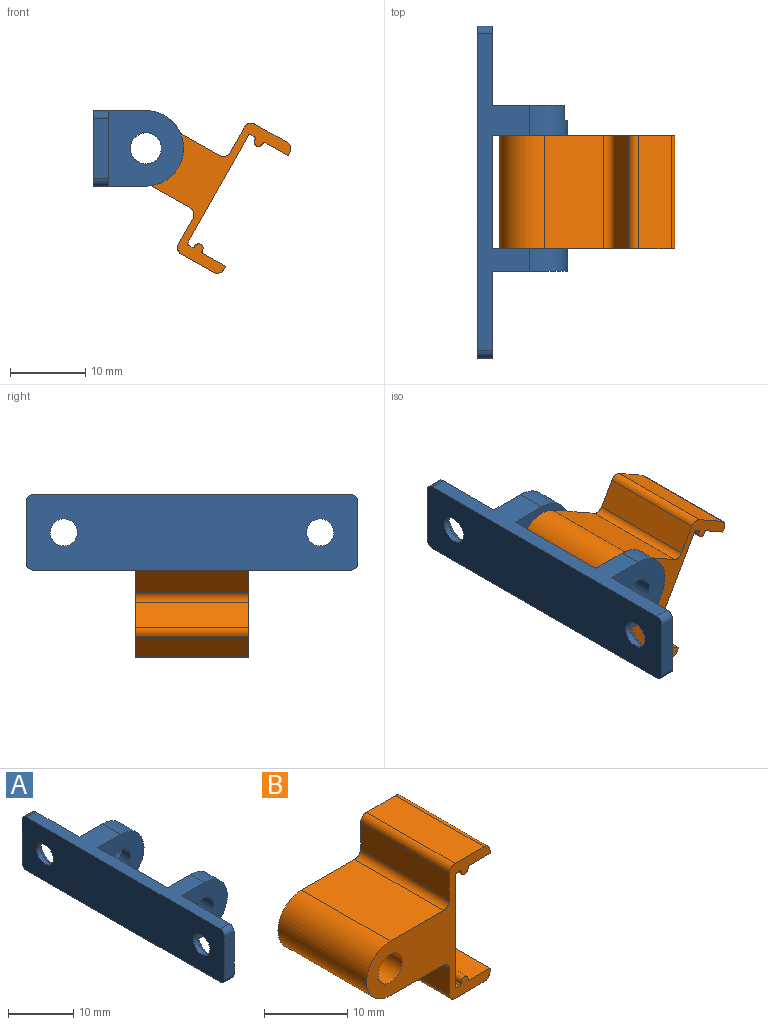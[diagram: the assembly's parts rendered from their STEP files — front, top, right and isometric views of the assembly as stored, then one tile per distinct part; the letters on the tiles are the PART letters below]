
ASSEMBLY  parts=2 mates=1
PART A: 32 faces, bbox 12x44x10 mm
  f0: plane 15.05x10mm, normal (1,0,0), area 150.5mm2, adj f3,f7,f17,f29
  f1: plane 10x9.58mm, normal (0,1,0), area 42.1mm2, adj f2,f3,f7,f18,f19,f20,f21,f22
  f2: plane 10.48x10mm, normal (1,0,0), area 76mm2, adj f1,f3,f7,f12,f13,f14,f16
  f3: plane 42x7mm, normal (0,0,1), area 119mm2, adj f0,f1,f2,f4,f8,f9,f12,f17
  f4: cylinder r=1mm len=2mm, axis (-1,0,0), area 3.1mm2, adj f3,f5,f8,f9
  f5: plane 8x2mm, normal (0,-1,0), area 16mm2, adj f4,f6,f8,f9
  f6: cylinder r=1mm len=2mm, axis (-1,0,0), area 3.1mm2, adj f5,f7,f8,f9
  f7: plane 42x7mm, normal (0,0,-1), area 119mm2, adj f0,f1,f2,f6,f8,f9,f14,f17
  f8: plane 11.48x10mm, normal (1,0,0), area 86mm2, adj f3,f4,f5,f6,f7,f11,f28
  f9: plane 44x10mm, normal (-1,0,0), area 418.8mm2, adj f3,f4,f5,f6,f7,f10,f12,f13
  f10: cylinder r=1.8mm len=3.6mm, axis (1,0,0), area 9mm2, adj f9,f11
  f11: cone r=1.8mm half-angle=45deg, axis (1,0,0), area 25.6mm2, adj f8,f10
  f12: cylinder r=1mm len=2mm, axis (-1,0,0), area 3.1mm2, adj f2,f3,f9,f13
  f13: plane 8x2mm, normal (0,1,0), area 16mm2, adj f2,f9,f12,f14
  f14: cylinder r=1mm len=2mm, axis (-1,0,0), area 3.1mm2, adj f2,f7,f9,f13
  f15: cylinder r=1.8mm len=3.6mm, axis (1,0,0), area 9mm2, adj f9,f16
  f16: cone r=1.8mm half-angle=45deg, axis (1,0,0), area 25.6mm2, adj f2,f15
  f17: plane 10x10mm, normal (0,-1,0), area 75.4mm2, adj f0,f3,f7,f26,f27
  f18: plane 3.46x2mm, normal (-0.5,0,-0.87), area 8mm2, adj f1,f19,f24,f25
  f19: plane 2x1.12mm, normal (0,0,-1), area 2.2mm2, adj f1,f18,f25,f27
  f20: plane 2x1.12mm, normal (0,0,1), area 2.2mm2, adj f1,f21,f25,f27
  f21: plane 3.46x2mm, normal (-0.5,0,0.87), area 8mm2, adj f1,f20,f22,f25
  f22: plane 3.46x2mm, normal (0.5,0,0.87), area 8mm2, adj f1,f21,f23,f25
  f23: plane 4x2mm, normal (1,0,0), area 8mm2, adj f1,f22,f24,f25
  f24: plane 3.46x2mm, normal (0.5,0,-0.87), area 8mm2, adj f1,f18,f23,f25
  f25: plane 8.46x8mm, normal (0,1,0), area 33.3mm2, adj f18,f19,f20,f21,f22,f23,f24,f26
  f26: cylinder r=2.1mm len=4.2mm, axis (0,1,0), area 26.4mm2, adj f17,f25
  f27: cylinder r=5mm len=10mm, axis (0,1,0), area 54.6mm2, adj f1,f3,f7,f17,f19,f20,f25
  f28: plane 10x10mm, normal (0,-1,0), area 75.4mm2, adj f3,f7,f8,f30,f31
  f29: plane 10x10mm, normal (0,1,0), area 75.4mm2, adj f0,f3,f7,f30,f31
  f30: cylinder r=5mm len=10mm, axis (0,1,0), area 47.1mm2, adj f3,f7,f28,f29
  f31: cylinder r=2.1mm len=4.2mm, axis (0,1,0), area 39.6mm2, adj f28,f29
PART B: 35 faces, bbox 20.9x15x19.8 mm
  f0: cylinder r=0.2mm len=15mm, axis (0,1,0), area 4.7mm2, adj f1,f32,f33,f34
  f1: plane 15x3.51mm, normal (0,0,-1), area 52.7mm2, adj f0,f2,f33,f34
  f2: plane 15x0.5mm, normal (1,0,0), area 7.5mm2, adj f1,f3,f33,f34
  f3: cylinder r=1mm len=15mm, axis (0,1,0), area 23.6mm2, adj f2,f4,f33,f34
  f4: plane 15x4.91mm, normal (0,0,1), area 73.6mm2, adj f3,f5,f33,f34
  f5: cylinder r=1mm len=15mm, axis (0,1,0), area 23.6mm2, adj f4,f6,f33,f34
  f6: plane 15x3.9mm, normal (-1,0,0), area 58.5mm2, adj f5,f7,f33,f34
  f7: cylinder r=1mm len=15mm, axis (0,1,0), area 23.6mm2, adj f6,f8,f33,f34
  f8: plane 15x9mm, normal (0,0,1), area 135mm2, adj f7,f9,f33,f34
  f9: cylinder r=4mm len=15mm, axis (0,1,0), area 188.5mm2, adj f8,f10,f33,f34
  f10: plane 15x9mm, normal (0,0,-1), area 135mm2, adj f9,f11,f33,f34
  f11: cylinder r=1mm len=15mm, axis (0,1,0), area 23.6mm2, adj f10,f12,f33,f34
  f12: plane 15x3.9mm, normal (-1,0,0), area 58.5mm2, adj f11,f13,f33,f34
  f13: cylinder r=1mm len=15mm, axis (0,1,0), area 23.6mm2, adj f12,f14,f33,f34
  f14: plane 15x4.91mm, normal (0,0,-1), area 73.6mm2, adj f13,f15,f33,f34
  f15: cylinder r=1mm len=15mm, axis (0,1,0), area 23.6mm2, adj f14,f16,f33,f34
  f16: plane 15x0.5mm, normal (1,0,0), area 7.5mm2, adj f15,f17,f33,f34
  f17: plane 15x3.51mm, normal (0,0,1), area 52.7mm2, adj f16,f18,f33,f34
  f18: cylinder r=0.2mm len=15mm, axis (0,1,0), area 4.7mm2, adj f17,f19,f33,f34
  f19: plane 15x0.1mm, normal (1,0,0), area 1.5mm2, adj f18,f20,f33,f34
  f20: cylinder r=0.6mm len=15mm, axis (0,1,0), area 28.3mm2, adj f19,f21,f33,f34
  f21: plane 15x0.1mm, normal (-1,0,0), area 1.5mm2, adj f20,f22,f33,f34
  f22: cylinder r=0.2mm len=15mm, axis (0,1,0), area 4.7mm2, adj f21,f23,f33,f34
  f23: plane 15x0.6mm, normal (0,0,1), area 9mm2, adj f22,f24,f33,f34
  f24: cylinder r=0.2mm len=15mm, axis (0,1,0), area 4.7mm2, adj f23,f25,f33,f34
  f25: plane 16.4x15mm, normal (1,0,0), area 246mm2, adj f24,f26,f33,f34
  f26: cylinder r=0.2mm len=15mm, axis (0,1,0), area 4.7mm2, adj f25,f27,f33,f34
  f27: plane 15x0.6mm, normal (0,0,-1), area 9mm2, adj f26,f28,f33,f34
  f28: cylinder r=0.2mm len=15mm, axis (0,1,0), area 4.7mm2, adj f27,f29,f33,f34
  f29: plane 15x0.1mm, normal (-1,0,0), area 1.5mm2, adj f28,f30,f33,f34
  f30: cylinder r=0.6mm len=15mm, axis (0,1,0), area 28.3mm2, adj f29,f32,f33,f34
  f31: cylinder r=2.05mm len=15mm, axis (0,1,0), area 193.2mm2, adj f33,f34
  f32: plane 15x0.1mm, normal (1,0,0), area 1.5mm2, adj f0,f30,f33,f34
  f33: plane 20.91x19.8mm, normal (0,-1,0), area 130.9mm2, adj f0,f1,f2,f3,f4,f5,f6,f7
  f34: plane 20.91x19.8mm, normal (0,1,0), area 130.9mm2, adj f0,f1,f2,f3,f4,f5,f6,f7
PLACE A t=(-16.92,0.61,8.6)mm
PLACE B rot(axis=(0,1,0),29.5deg) t=(-1.21,8.09,8.68)mm
MATE revolute A.f26 <-> B.f31  axis (0,1,0) through (-9.92,-6.91,13.6)mm
